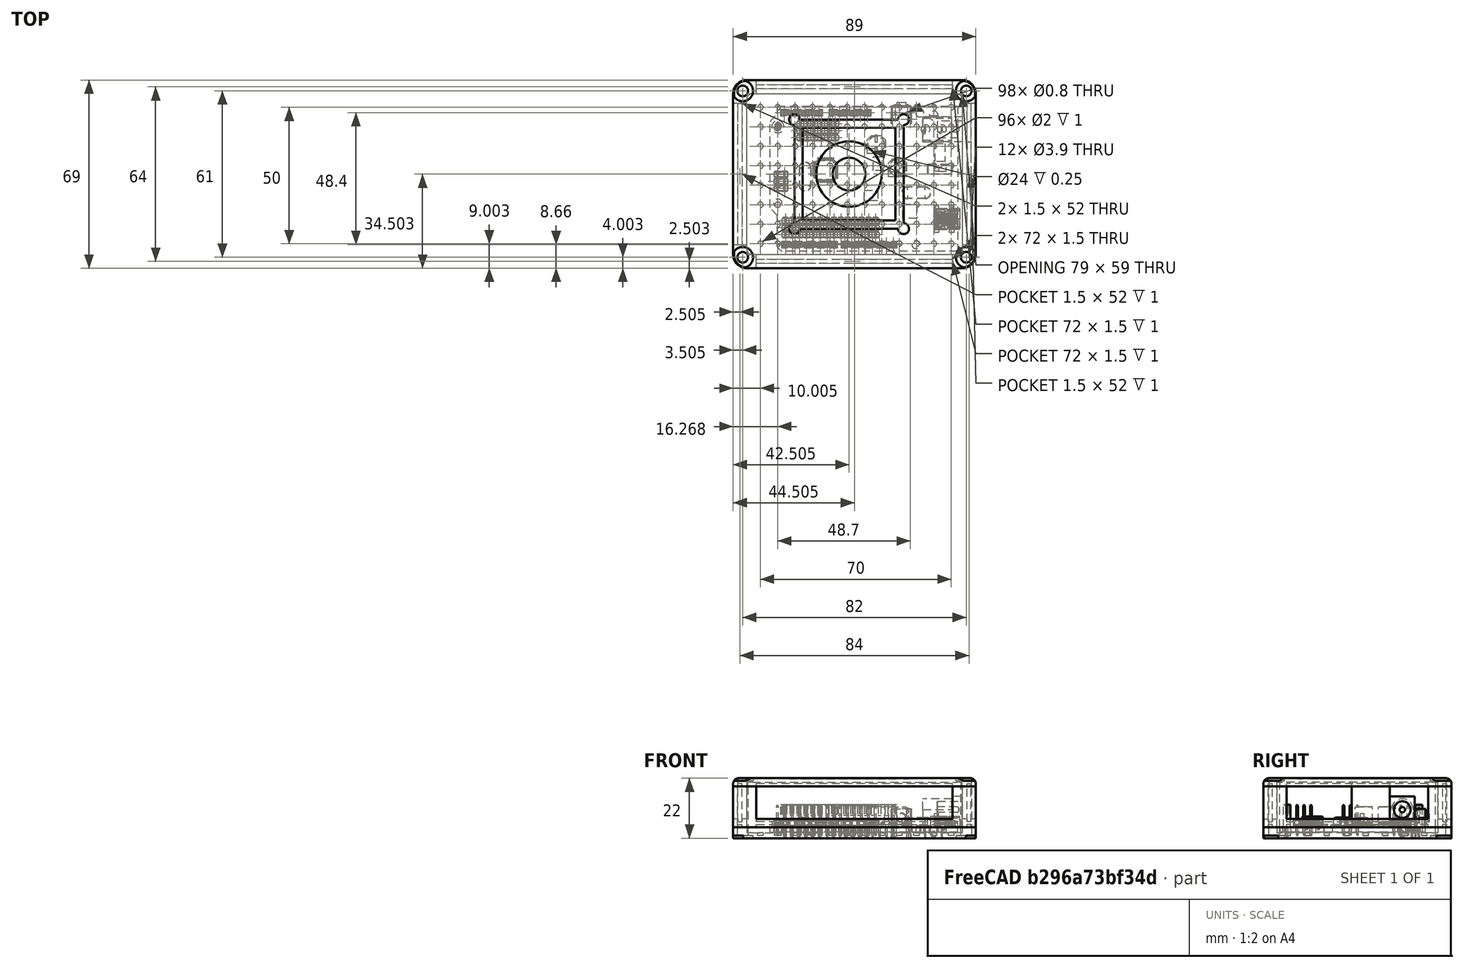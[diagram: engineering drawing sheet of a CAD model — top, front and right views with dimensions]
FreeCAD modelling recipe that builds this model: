
FCSTD DOCUMENT  (FreeCAD 0.16R)
Label: assembly
License: All rights reserved
LicenseURL: http://en.wikipedia.org/wiki/All_rights_reserved
objects: App::FeaturePython×18, Part::Box×4, Part::Feature×3, Part::FeaturePython×2
note: 9 computed .brp shape members not serialized (recipe doc carries the construction recipe); baked Part::Feature solids carry a one-line shape summary decoded from their .brp

FEATURE [Part::Feature] Pocket004001  label="Frame"
  Placement = pos=(214.965,9.85313,36.5996) rot=(0,0,1;0rad)
  shape: bbox 89 x 69 x 15 mm, 81 faces (baked)
FEATURE [Part::Box] Box  label="Wall"
  Height = 14
  Length = 72
  Placement = pos=(178.965,41.1031,38.5996) rot=(0,0,1;0rad)
  Width = 1.5
FEATURE [Part::Box] Box001  label="Wall001"
  Height = 14
  Length = 52
  Placement = pos=(172.215,35.8531,38.5996) rot=(0,0,-1;1.5708rad)
  Width = 1.5
FEATURE [Part::Box] Box002  label="Wall002"
  Height = 14
  Length = 72
  Placement = pos=(178.965,-22.8969,38.5996) rot=(0,0,1;0rad)
  Width = 1.5
FEATURE [Part::Box] Box003  label="Wall003"
  Height = 14
  Length = 14
  Placement = pos=(256.215,21.7383,38.5996) rot=(0,0,-1;1.5708rad)
  Width = 1.5
FEATURE [Part::Feature] Pad001001  label="Top"
  Placement = pos=(170.465,-24.6469,51.5996) rot=(0,0,1;0rad)
  shape: bbox 89.82 x 69.82 x 3.42 mm, 79 faces (baked)
FEATURE [Part::Feature] MultiTransform001  label="Bottom"
  Placement = pos=(170.465,-24.6469,32.5996) rot=(0,0,1;0rad)
  shape: bbox 89 x 69 x 5 mm, 245 faces (baked)
FEATURE [Part::FeaturePython] freaduino_uno_01  # a2plus imported part (geometry in sourceFile) (typed FeaturePython)
  Placement = pos=(252.829,34.8103,34.8996) rot=(0,0,1;3.14159rad)
  fixedPosition = true
  sourceFile = <userpath>/Загрузки/freaduino-uno.fcstd
  timeLastImport = 1.54422e+09
  updateColors = true
FEATURE [Part::FeaturePython] Screw  label="M2.5x3-Screw"  # Fasteners workbench fastener (typed FeaturePython)
  Placement = pos=(186.829,27.2103,36.5996) rot=(0,0,1;0rad)
  diameter = 1
  invert = false
  length = 0
  matchOuter = false
  offset = 0
  thread = false
  type = 19
FEATURE [App::FeaturePython] circularEdgeConstraint01  label="circularEdgeConstraint01__M2.5x3-Screw"  # a2plus constraint (typed FeaturePython)
  Object1 = freaduino_uno_01
  Object2 = Screw
  SubElement1 = Edge128
  SubElement2 = Edge66
  Type = circularEdge
  directionConstraint = 0
  lockRotation = false
  offset = 0
FEATURE [App::FeaturePython] circularEdgeConstraint01_mirror  label="circularEdgeConstraint01__freaduino_uno_01"  # a2plus constraint (typed FeaturePython)
  Object1 = freaduino_uno_01
  Object2 = Screw
  SubElement1 = Edge128
  SubElement2 = Edge66
  Type = circularEdge
  directionConstraint = 0
  lockRotation = false
  offset = 0
FEATURE [App::FeaturePython] circularEdgeConstraint02  # a2plus constraint (typed FeaturePython)
  Object1 = MultiTransform001
  Object2 = Screw
  SubElement1 = Edge382
  SubElement2 = Edge71
  Type = circularEdge
  directionConstraint = 0
  lockRotation = false
  offset = 0
FEATURE [App::FeaturePython] circularEdgeConstraint03  # a2plus constraint (typed FeaturePython)
  Object1 = Pocket004001
  Object2 = MultiTransform001
  SubElement1 = Edge25
  SubElement2 = Edge49
  Type = circularEdge
  directionConstraint = 0
  lockRotation = false
  offset = 0
FEATURE [App::FeaturePython] planeConstraint01  # a2plus constraint (typed FeaturePython)
  Object1 = Box
  Object2 = Pocket004001
  SubElement1 = Face2
  SubElement2 = Face53
  Type = plane
  directionConstraint = 1
  offset = 0
FEATURE [App::FeaturePython] planeConstraint02  # a2plus constraint (typed FeaturePython)
  Object1 = Pocket004001
  Object2 = Box
  SubElement1 = Face79
  SubElement2 = Face5
  Type = plane
  directionConstraint = 0
  offset = 0
FEATURE [App::FeaturePython] planeConstraint03  # a2plus constraint (typed FeaturePython)
  Object1 = Pocket004001
  Object2 = Box
  SubElement1 = Face72
  SubElement2 = Face4
  Type = plane
  directionConstraint = 1
  offset = 0
FEATURE [App::FeaturePython] planeConstraint04  # a2plus constraint (typed FeaturePython)
  Object1 = Box002
  Object2 = Pocket004001
  SubElement1 = Face2
  SubElement2 = Face50
  Type = plane
  directionConstraint = 1
  offset = 0
FEATURE [App::FeaturePython] planeConstraint05  # a2plus constraint (typed FeaturePython)
  Object1 = Pocket004001
  Object2 = Box002
  SubElement1 = Face80
  SubElement2 = Face5
  Type = plane
  directionConstraint = 0
  offset = 0
FEATURE [App::FeaturePython] planeConstraint06  # a2plus constraint (typed FeaturePython)
  Object1 = Pocket004001
  Object2 = Box002
  SubElement1 = Face76
  SubElement2 = Face4
  Type = plane
  directionConstraint = 0
  offset = 0
FEATURE [App::FeaturePython] planeConstraint07  # a2plus constraint (typed FeaturePython)
  Object1 = Box001
  Object2 = Pocket004001
  SubElement1 = Face2
  SubElement2 = Face7
  Type = plane
  directionConstraint = 1
  offset = 0
FEATURE [App::FeaturePython] planeConstraint08  # a2plus constraint (typed FeaturePython)
  Object1 = Pocket004001
  Object2 = Box001
  SubElement1 = Face67
  SubElement2 = Face5
  Type = plane
  directionConstraint = 0
  offset = 0
FEATURE [App::FeaturePython] planeConstraint09  # a2plus constraint (typed FeaturePython)
  Object1 = Pocket004001
  Object2 = Box001
  SubElement1 = Face46
  SubElement2 = Face3
  Type = plane
  directionConstraint = 0
  offset = 0
FEATURE [App::FeaturePython] planeConstraint10  # a2plus constraint (typed FeaturePython)
  Object1 = Pocket004001
  Object2 = Box003
  SubElement1 = Face78
  SubElement2 = Face3
  Type = plane
  directionConstraint = 0
  offset = 0
FEATURE [App::FeaturePython] planeConstraint11  # a2plus constraint (typed FeaturePython)
  Object1 = Pocket004001
  Object2 = Box003
  SubElement1 = Face81
  SubElement2 = Face5
  Type = plane
  directionConstraint = 0
  offset = 0
FEATURE [App::FeaturePython] planeConstraint12  label="planeConstraint12__Wall003"  # a2plus constraint (typed FeaturePython)
  Object1 = freaduino_uno_01
  Object2 = Box003
  SubElement1 = Face2947
  SubElement2 = Face1
  Type = plane
  directionConstraint = 0
  offset = 0
FEATURE [App::FeaturePython] planeConstraint12_mirror  label="planeConstraint12__freaduino_uno_01"  # a2plus constraint (typed FeaturePython)
  Object1 = freaduino_uno_01
  Object2 = Box003
  SubElement1 = Face2947
  SubElement2 = Face1
  Type = plane
  directionConstraint = 0
  offset = 0
FEATURE [App::FeaturePython] circularEdgeConstraint04  # a2plus constraint (typed FeaturePython)
  Object1 = Pocket004001
  Object2 = Pad001001
  SubElement1 = Edge115
  SubElement2 = Edge101
  Type = circularEdge
  directionConstraint = 1
  lockRotation = false
  offset = 0
